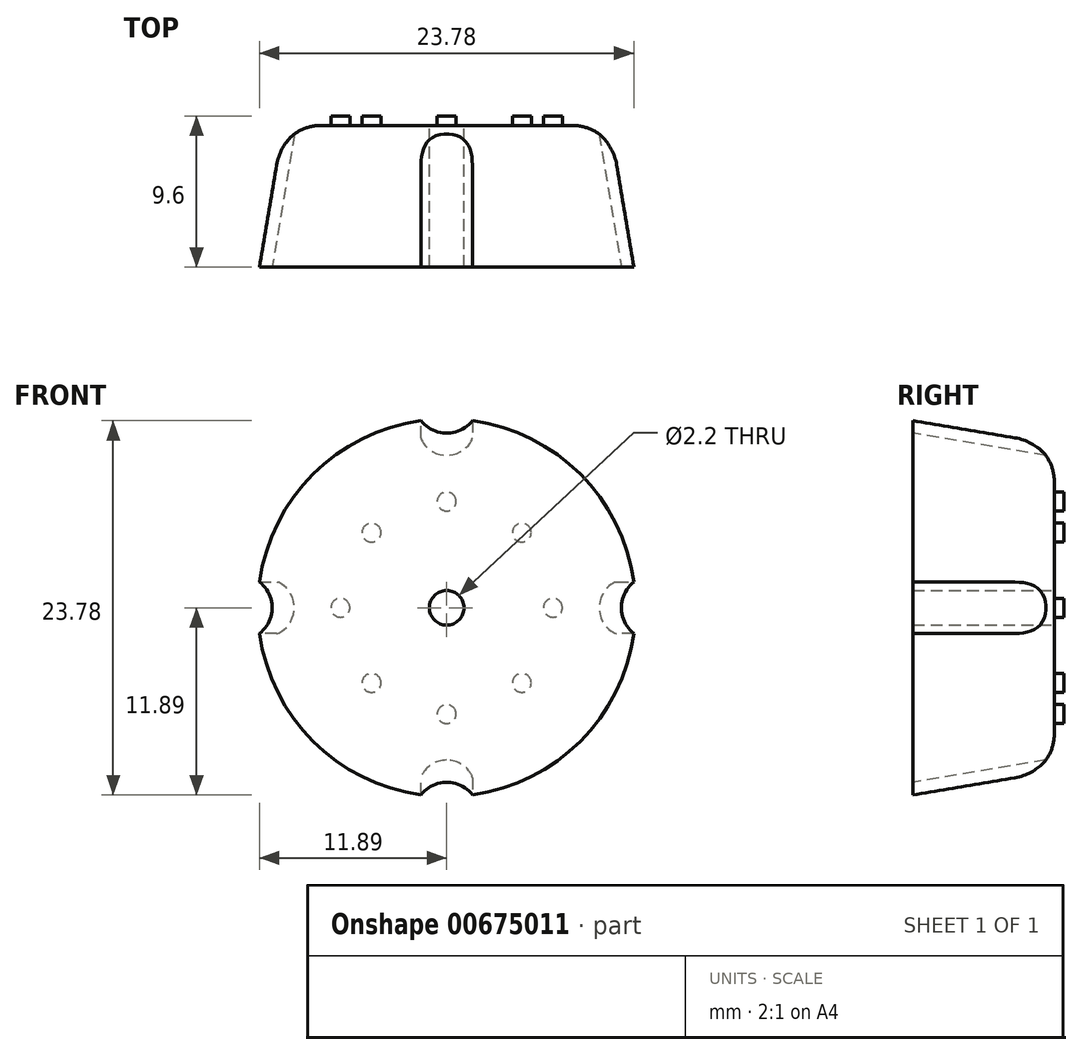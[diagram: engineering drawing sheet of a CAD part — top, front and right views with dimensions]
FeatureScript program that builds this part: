
annotation { "Feature Type Name" : "Feature", "Feature Type Description" : "" }
export const myFeature = defineFeature(function(context is Context, id is Id, definition is map)
    precondition{}
    {
        {
            assignVariable(context, id + "F0", {"name" : "Faktor", "anyValue" : 1.5});
        }
        {
            var Q0;
            Q0=qCreatedBy(makeId("Top.planeOp"),FACE);
            var sketch = newSketch(context, id + "F1", { "sketchPlane" : qUnion([Q0])});
            skLineSegment(sketch, "E0", {"start": v(0, 0) * mm, "end": v(0, 26.8) * mm, "construction": true});
            skLineSegment(sketch, "E1", {"start": v(0, 0) * mm, "end": v(-12, 0) * mm});
            skLineSegment(sketch, "E2", {"start": v(-12, 0) * mm, "end": v(-10.92, 6.5) * mm});
            skLineSegment(sketch, "E3", {"start": v(-7.96, 9) * mm, "end": v(0, 9) * mm});
            skLineSegment(sketch, "E4", {"start": v(0, 9) * mm, "end": v(0, 0) * mm});
            skPoint(sketch, "E5.visualSharp", {"position": v(-10.5, 9) * mm});
            skArc(sketch, "E5.filletArc", {"start": v(-7.96, 9) * mm, "mid": v(-9.9, 8.29) * mm, "end": v(-10.92, 6.5) * mm});
            skSolve(sketch);
        }
        {
            var Q0;
            Q0=qSketchRegion(id+"F1",true);
            var Q1;
            Q1=sQuery(id+"F1.wireOp",EDGE,"E0");
            revolve(context, id + "F2", {"entities" : qUnion([Q0]), "axis" : qUnion([Q1]), "revolveType" : RevolveType.FULL});
        }
        {
            var Q0;
            Q0=makeQuery(id+"F2.opRevolve","SWEPT_FACE",FACE,{"disambiguationData":[OSD([sQuery(id+"F1.wireOp",EDGE,"E3")])]});
            var sketch = newSketch(context, id + "F3", { "sketchPlane" : qUnion([Q0])});
            skCircle(sketch, "E6", {"center": v(0, 0) * mm, "radius": 6.75 * mm, "construction": true});
            skCircle(sketch, "E7", {"center": v(0, 6.75) * mm, "radius": 0.6 * mm});
            skCircle(sketch, "E8", {"center": v(6.75, 0) * mm, "radius": 0.6 * mm});
            skCircle(sketch, "E9", {"center": v(0, -6.75) * mm, "radius": 0.6 * mm});
            skCircle(sketch, "E10", {"center": v(-6.75, 0) * mm, "radius": 0.6 * mm});
            skLineSegment(sketch, "E11", {"start": v(-6.52, 6.52) * mm, "end": v(7.02, -7.02) * mm, "construction": true});
            skLineSegment(sketch, "E12", {"start": v(-6.76, -6.76) * mm, "end": v(6.87, 6.87) * mm, "construction": true});
            skCircle(sketch, "E13", {"center": v(-4.77, 4.77) * mm, "radius": 0.6 * mm});
            skCircle(sketch, "E14", {"center": v(4.77, 4.77) * mm, "radius": 0.6 * mm});
            skCircle(sketch, "E15", {"center": v(4.77, -4.77) * mm, "radius": 0.6 * mm});
            skCircle(sketch, "E16", {"center": v(-4.77, -4.77) * mm, "radius": 0.6 * mm});
            skSolve(sketch);
        }
        {
            var Q0;
            Q0=qSketchRegion(id+"F3",true);
            extrude(context, id + "F4", {"entities" : qUnion([Q0]), "operationType" : NewBodyOperationType.ADD, "depth" : getVariable(context, 'Faktor') * 0.4 * mm, "offsetDistance" : 25 * mm});
        }
        {
            var Q0;
            Q0=qCreatedBy(makeId("Right.planeOp"),FACE);
            var sketch = newSketch(context, id + "F5", { "sketchPlane" : qUnion([Q0])});
            skLineSegment(sketch, "E17", {"start": v(-0.89, 13.36) * mm, "end": v(13.36, 11) * mm, "construction": true});
            skLineSegment(sketch, "E18", {"start": v(0.65, 11.9) * mm, "end": v(4.98, 11.17) * mm, "construction": true});
            skLineSegment(sketch, "E19", {"start": v(4.98, -11.17) * mm, "end": v(0.65, -11.9) * mm, "construction": true});
            skLineSegment(sketch, "E20.0", {"start": v(6.5, -10.92) * mm, "end": v(6.5, 10.92) * mm, "construction": true});
            skLineSegment(sketch, "E21", {"start": v(0, 13.22) * mm, "end": v(0.35, 15.29) * mm});
            skLineSegment(sketch, "E22", {"start": v(0.35, 15.29) * mm, "end": v(9.35, 13.79) * mm});
            skLineSegment(sketch, "E23", {"start": v(9.35, 13.79) * mm, "end": v(9, 11.72) * mm});
            skLineSegment(sketch, "E24", {"start": v(9, 11.72) * mm, "end": v(0, 13.22) * mm});
            skSolve(sketch);
        }
        {
            var Q0;
            Q0=qSketchRegion(id+"F5",true);
            var Q1;
            Q1=sQuery(id+"F5.wireOp",EDGE,"E17");
            revolve(context, id + "F6", {"entities" : qUnion([Q0]), "axis" : qUnion([Q1]), "revolveType" : RevolveType.FULL});
        }
        {
            var Q0;
            Q0=makeQuery(id+"F6.opRevolve","SWEPT_BODY",BODY,{"disambiguationData":[OSD([sQuery(id+"F5.wireOp",EDGE,"E21"),sQuery(id+"F5.wireOp",EDGE,"E22"),sQuery(id+"F5.wireOp",EDGE,"E23"),sQuery(id+"F5.wireOp",EDGE,"E24")])]});
            var Q1;
            Q1=makeQuery(id+"F2.opRevolve","SWEPT_EDGE",EDGE,{"disambiguationData":[OSD([sQuery(id+"F1.wireOp",EDGE,"E1"),sQuery(id+"F1.wireOp",EDGE,"E2")])]});
            circularPattern(context, id + "F7", {"entities" : qUnion([Q0]), "axis" : qUnion([Q1]), "angle" : 360 * degree, "instanceCount" : 4, "equalSpace" : true});
        }
        {
            var Q0;
            Q0=makeQuery(id+"F6.opRevolve","SWEPT_BODY",BODY,{"disambiguationData":[OSD([sQuery(id+"F5.wireOp",EDGE,"E21"),sQuery(id+"F5.wireOp",EDGE,"E22"),sQuery(id+"F5.wireOp",EDGE,"E23"),sQuery(id+"F5.wireOp",EDGE,"E24")])]});
            var Q1;
            Q1=makeQuery(id+"F7.opPattern","COPY",BODY,{"derivedFrom":makeQuery(id+"F6.opRevolve","SWEPT_BODY",BODY,{"disambiguationData":[OSD([sQuery(id+"F5.wireOp",EDGE,"E21"),sQuery(id+"F5.wireOp",EDGE,"E22"),sQuery(id+"F5.wireOp",EDGE,"E23"),sQuery(id+"F5.wireOp",EDGE,"E24")])]}),"instanceName":"1"});
            var Q2;
            Q2=makeQuery(id+"F7.opPattern","COPY",BODY,{"derivedFrom":makeQuery(id+"F6.opRevolve","SWEPT_BODY",BODY,{"disambiguationData":[OSD([sQuery(id+"F5.wireOp",EDGE,"E21"),sQuery(id+"F5.wireOp",EDGE,"E22"),sQuery(id+"F5.wireOp",EDGE,"E23"),sQuery(id+"F5.wireOp",EDGE,"E24")])]}),"instanceName":"2"});
            var Q3;
            Q3=makeQuery(id+"F7.opPattern","COPY",BODY,{"derivedFrom":makeQuery(id+"F6.opRevolve","SWEPT_BODY",BODY,{"disambiguationData":[OSD([sQuery(id+"F5.wireOp",EDGE,"E21"),sQuery(id+"F5.wireOp",EDGE,"E22"),sQuery(id+"F5.wireOp",EDGE,"E23"),sQuery(id+"F5.wireOp",EDGE,"E24")])]}),"instanceName":"3"});
            var Q4;
            Q4=makeQuery(id+"F2.opRevolve","SWEPT_BODY",BODY,{"disambiguationData":[OSD([sQuery(id+"F1.wireOp",EDGE,"E1"),sQuery(id+"F1.wireOp",EDGE,"E2"),sQuery(id+"F1.wireOp",EDGE,"E3"),sQuery(id+"F1.wireOp",EDGE,"E4"),sQuery(id+"F1.wireOp",EDGE,"E5.filletArc")])]});
            booleanBodies(context, id + "F8", {"operationType" : BooleanOperationType.SUBTRACTION, "tools" : qUnion([Q0, Q1, Q2, Q3]), "targets" : qUnion([Q4])});
        }
        {
            var Q0;
            Q0=makeQuery(id+"F2.opRevolve","SWEPT_FACE",FACE,{"disambiguationData":[OSD([sQuery(id+"F1.wireOp",EDGE,"E3")])]});
            var sketch = newSketch(context, id + "F9", { "sketchPlane" : qUnion([Q0])});
            skCircle(sketch, "E25", {"center": v(0, 0) * mm, "radius": 1.1 * mm});
            skSolve(sketch);
        }
        {
            var Q0;
            Q0=qSketchRegion(id+"F9",true);
            extrude(context, id + "F10", {"entities" : qUnion([Q0]), "operationType" : NewBodyOperationType.REMOVE, "endBound" : BoundingType.THROUGH_ALL, "oppositeDirection" : true, "depth" : 25 * mm, "offsetDistance" : 25 * mm});
        }
    });
